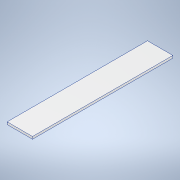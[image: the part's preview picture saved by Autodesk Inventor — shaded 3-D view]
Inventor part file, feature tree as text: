
AUTODESK INVENTOR PART (.ipt)
format: ipt  version: 2021 (Build 250183000, 183)  size: 125,440 bytes
history: native  units: mm
features: other x1, extrude x1, sketch x1
ambient origin geometry x8: Origin, YZ Plane, XZ Plane, XY Plane, X Axis, Y Axis, Z Axis, Center Point
bodies: Body1 (feature_tree)
feature tree (3):
  other  "實體1"
  extrude  "擠出1"  Depth=32.0mm
  sketch  "草圖1"
